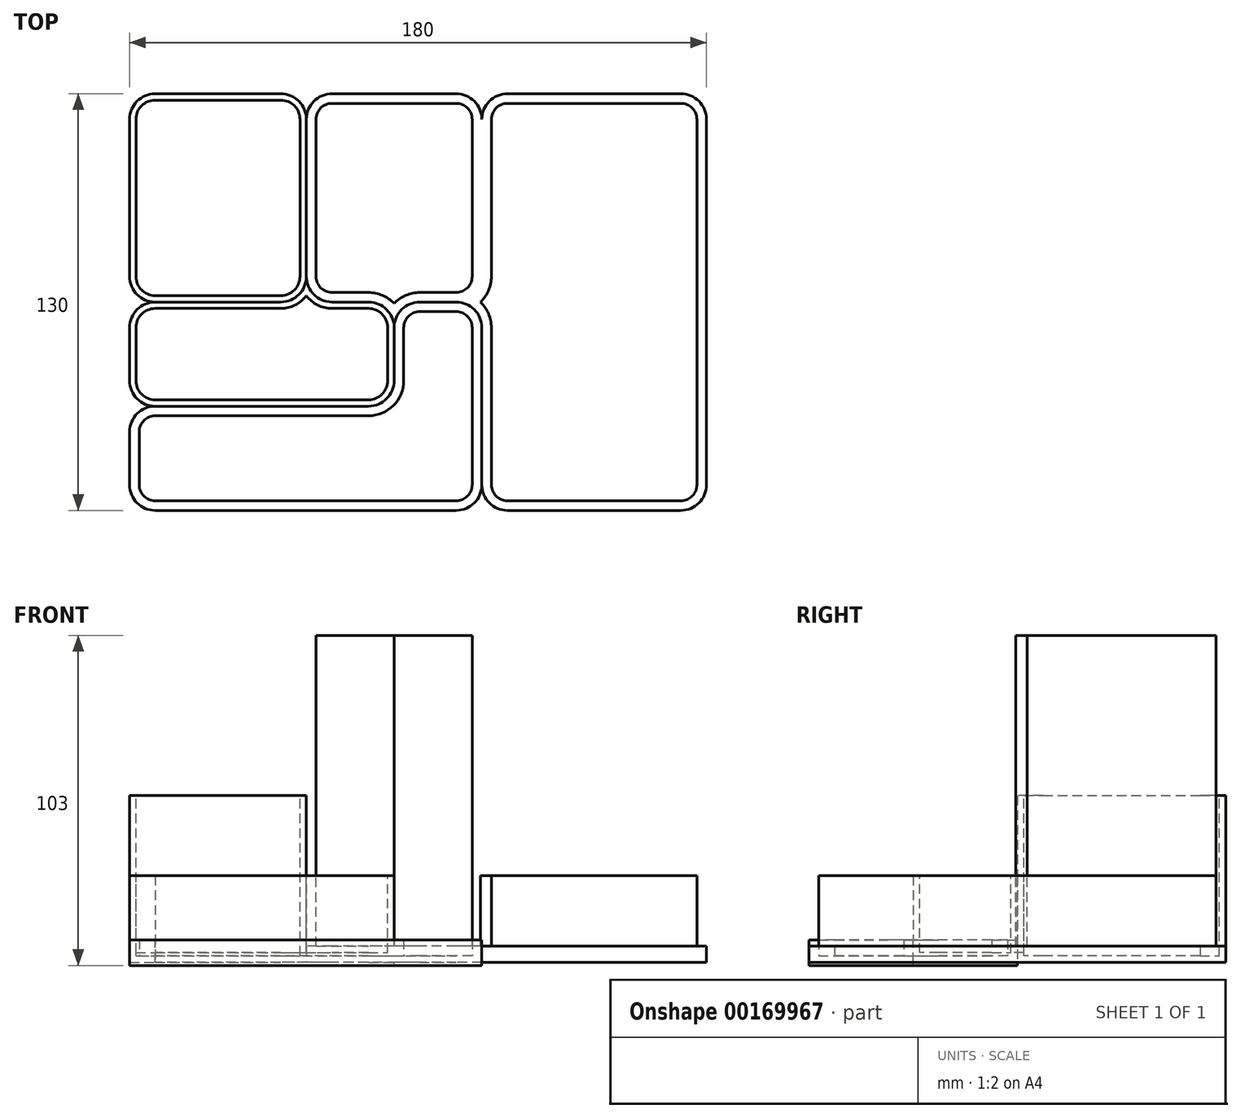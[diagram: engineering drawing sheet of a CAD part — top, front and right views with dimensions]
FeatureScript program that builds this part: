
annotation { "Feature Type Name" : "Feature", "Feature Type Description" : "" }
export const myFeature = defineFeature(function(context is Context, id is Id, definition is map)
    precondition{}
    {
        {
            var Q0;
            Q0=qCreatedBy(makeId("Top.planeOp"),FACE);
            var sketch = newSketch(context, id + "F0", { "sketchPlane" : qUnion([Q0])});
            skLineSegment(sketch, "E0.bottom", {"start": v(11.9, -65) * mm, "end": v(-82, -65) * mm});
            skLineSegment(sketch, "E0.top", {"start": v(82, 65) * mm, "end": v(27.9, 65) * mm});
            skLineSegment(sketch, "E0.left", {"start": v(90, -57) * mm, "end": v(90, 57) * mm});
            skLineSegment(sketch, "E0.right", {"start": v(-90, 8) * mm, "end": v(-90, 57) * mm});
            skPoint(sketch, "E0.middle", {"position": v(0, 0) * mm});
            skPoint(sketch, "E1.visualSharp", {"position": v(-90, 65) * mm});
            skArc(sketch, "E1.filletArc", {"start": v(-82, 65) * mm, "mid": v(-87.66, 62.66) * mm, "end": v(-90, 57) * mm});
            skPoint(sketch, "E2.visualSharp", {"position": v(90, 65) * mm});
            skArc(sketch, "E2.filletArc", {"start": v(90, 57) * mm, "mid": v(87.66, 62.66) * mm, "end": v(82, 65) * mm});
            skPoint(sketch, "E3.visualSharp", {"position": v(90, -65) * mm});
            skArc(sketch, "E3.filletArc", {"start": v(82, -65) * mm, "mid": v(87.66, -62.66) * mm, "end": v(90, -57) * mm});
            skPoint(sketch, "E4.visualSharp", {"position": v(-90, -65) * mm});
            skArc(sketch, "E4.filletArc", {"start": v(-90, -57) * mm, "mid": v(-87.66, -62.66) * mm, "end": v(-82, -65) * mm});
            skLineSegment(sketch, "E5", {"start": v(-34.83, 57) * mm, "end": v(-34.83, 8) * mm});
            skLineSegment(sketch, "E6", {"start": v(-82, 0) * mm, "end": v(-42.83, 0) * mm});
            skLineSegment(sketch, "E7", {"start": v(-26.83, 0) * mm, "end": v(-15.46, 0) * mm});
            skLineSegment(sketch, "E8", {"start": v(19.9, 8) * mm, "end": v(19.9, 57) * mm});
            skPoint(sketch, "E9.visualSharp", {"position": v(-34.83, 0) * mm});
            skArc(sketch, "E9.filletArc", {"start": v(-42.83, 0) * mm, "mid": v(-37.17, 2.34) * mm, "end": v(-34.83, 8) * mm});
            skArc(sketch, "E10.filletArc", {"start": v(-34.83, 8) * mm, "mid": v(-32.49, 2.34) * mm, "end": v(-26.83, 0) * mm});
            skPoint(sketch, "E11.visualSharp", {"position": v(19.9, 0) * mm});
            skArc(sketch, "E11.filletArc", {"start": v(11.9, 0) * mm, "mid": v(17.56, 2.34) * mm, "end": v(19.9, 8) * mm});
            skArc(sketch, "E12.filletArc", {"start": v(27.9, 65) * mm, "mid": v(22.24, 62.66) * mm, "end": v(19.9, 57) * mm});
            skLineSegment(sketch, "E13", {"start": v(-82, 65) * mm, "end": v(-42.83, 65) * mm});
            skArc(sketch, "E14.filletArc", {"start": v(19.9, 57) * mm, "mid": v(17.56, 62.66) * mm, "end": v(11.9, 65) * mm});
            skPoint(sketch, "E15.newPointA", {"position": v(-90, -57) * mm});
            skPoint(sketch, "E15.newPointB", {"position": v(-90, 0) * mm});
            skArc(sketch, "E15.filletArc", {"start": v(-90, 8) * mm, "mid": v(-87.66, 2.34) * mm, "end": v(-82, 0) * mm});
            skLineSegment(sketch, "E16", {"start": v(-90, -24.5) * mm, "end": v(-90, -8) * mm});
            skArc(sketch, "E17.filletArc", {"start": v(-82, 0) * mm, "mid": v(-87.66, -2.34) * mm, "end": v(-90, -8) * mm});
            skArc(sketch, "E18.filletArc", {"start": v(-34.83, 57) * mm, "mid": v(-37.17, 62.66) * mm, "end": v(-42.83, 65) * mm});
            skLineSegment(sketch, "E19", {"start": v(11.9, 65) * mm, "end": v(-26.83, 65) * mm});
            skArc(sketch, "E20.filletArc", {"start": v(-26.83, 65) * mm, "mid": v(-32.49, 62.66) * mm, "end": v(-34.83, 57) * mm});
            skLineSegment(sketch, "E21", {"start": v(-82, -32.5) * mm, "end": v(-15.46, -32.5) * mm});
            skPoint(sketch, "E22.visualSharp", {"position": v(19.9, -32.5) * mm});
            skPoint(sketch, "E23.newPointA", {"position": v(-90, -32.5) * mm});
            skArc(sketch, "E23.filletArc", {"start": v(-90, -24.5) * mm, "mid": v(-87.66, -30.16) * mm, "end": v(-82, -32.5) * mm});
            skLineSegment(sketch, "E24", {"start": v(-90, -57) * mm, "end": v(-90, -40.5) * mm});
            skArc(sketch, "E25.filletArc", {"start": v(-82, -32.5) * mm, "mid": v(-87.66, -34.84) * mm, "end": v(-90, -40.5) * mm});
            skLineSegment(sketch, "E26", {"start": v(-7.46, -8) * mm, "end": v(-7.46, -24.5) * mm});
            skPoint(sketch, "E27.visualSharp", {"position": v(-7.46, -32.5) * mm});
            skArc(sketch, "E27.filletArc", {"start": v(-15.46, -32.5) * mm, "mid": v(-9.8, -30.16) * mm, "end": v(-7.46, -24.5) * mm});
            skPoint(sketch, "E28.newPointA", {"position": v(-7.46, 0) * mm});
            skPoint(sketch, "E28.newPointB", {"position": v(11.9, 0) * mm});
            skArc(sketch, "E28.filletArc", {"start": v(-7.46, -8) * mm, "mid": v(-9.8, -2.34) * mm, "end": v(-15.46, 0) * mm});
            skLineSegment(sketch, "E29", {"start": v(11.9, 0) * mm, "end": v(0.54, 0) * mm});
            skArc(sketch, "E30.filletArc", {"start": v(0.54, 0) * mm, "mid": v(-5.12, -2.34) * mm, "end": v(-7.46, -8) * mm});
            skLineSegment(sketch, "E31", {"start": v(19.9, -8) * mm, "end": v(19.9, -57) * mm});
            skArc(sketch, "E32.filletArc", {"start": v(19.9, -8) * mm, "mid": v(17.56, -2.34) * mm, "end": v(11.9, 0) * mm});
            skArc(sketch, "E33.filletArc", {"start": v(11.9, -65) * mm, "mid": v(17.56, -62.66) * mm, "end": v(19.9, -57) * mm});
            skLineSegment(sketch, "E34", {"start": v(82, -65) * mm, "end": v(27.9, -65) * mm});
            skArc(sketch, "E35.filletArc", {"start": v(19.9, -57) * mm, "mid": v(22.24, -62.66) * mm, "end": v(27.9, -65) * mm});
            skSolve(sketch);
        }
        {
            var Q0;
            Q0=makeQuery(id+"F0.imprint","IMPRINT",FACE,{"disambiguationData":[TD([[makeQuery(id+"F0.imprint","IMPRINT",EDGE,{"derivedFrom":sQuery(id+"F0.wireOp",EDGE,"E0.bottom")}),-1.0]])]});
            extrude(context, id + "F1", {"entities" : qUnion([Q0]), "oppositeDirection" : true, "depth" : 3 * mm});
        }
        {
            var Q0;
            Q0=makeQuery(id+"F0.imprint","IMPRINT",FACE,{"disambiguationData":[TD([[makeQuery(id+"F0.imprint","IMPRINT",EDGE,{"derivedFrom":sQuery(id+"F0.wireOp",EDGE,"E0.right")}),-1.0]])]});
            extrude(context, id + "F2", {"entities" : qUnion([Q0]), "depth" : 50 * mm});
        }
        {
            var Q0;
            Q0=makeQuery(id+"F0.imprint","IMPRINT",FACE,{"disambiguationData":[TD([[makeQuery(id+"F0.imprint","IMPRINT",EDGE,{"derivedFrom":sQuery(id+"F0.wireOp",EDGE,"E5")}),1.0]])]});
            extrude(context, id + "F3", {"entities" : qUnion([Q0]), "operationType" : NewBodyOperationType.ADD, "depth" : 100 * mm});
        }
        {
            var Q0;
            Q0=makeQuery(id+"F0.imprint","IMPRINT",FACE,{"disambiguationData":[TD([[makeQuery(id+"F0.imprint","IMPRINT",EDGE,{"derivedFrom":sQuery(id+"F0.wireOp",EDGE,"E6")}),-1.0]])]});
            extrude(context, id + "F4", {"entities" : qUnion([Q0]), "operationType" : NewBodyOperationType.ADD, "depth" : 25 * mm});
        }
        {
            var Q0;
            Q0=makeQuery(id+"F0.imprint","IMPRINT",FACE,{"disambiguationData":[TD([[makeQuery(id+"F0.imprint","IMPRINT",EDGE,{"derivedFrom":sQuery(id+"F0.wireOp",EDGE,"E0.top")}),1.0]])]});
            extrude(context, id + "F5", {"entities" : qUnion([Q0]), "operationType" : NewBodyOperationType.ADD, "depth" : 25 * mm});
        }
        {
            var Q0;
            Q0=makeQuery(id+"F5.opExtrude","CAP_FACE",FACE,{"disambiguationData":[OSD([sQuery(id+"F0.wireOp",EDGE,"E0.top"),sQuery(id+"F0.wireOp",EDGE,"E0.left"),sQuery(id+"F0.wireOp",EDGE,"E2.filletArc"),sQuery(id+"F0.wireOp",EDGE,"E3.filletArc"),sQuery(id+"F0.wireOp",EDGE,"E8"),sQuery(id+"F0.wireOp",EDGE,"E11.filletArc"),sQuery(id+"F0.wireOp",EDGE,"E12.filletArc"),sQuery(id+"F0.wireOp",EDGE,"E31"),sQuery(id+"F0.wireOp",EDGE,"E32.filletArc"),sQuery(id+"F0.wireOp",EDGE,"E34"),sQuery(id+"F0.wireOp",EDGE,"E35.filletArc")])],"isStart":false});
            var sketch = newSketch(context, id + "F6", { "sketchPlane" : qUnion([Q0])});
            skArc(sketch, "E36.0", {"start": v(22.9, 8) * mm, "mid": v(22, 3.64) * mm, "end": v(19.45, 0) * mm});
            skLineSegment(sketch, "E36.1", {"start": v(22.9, 57) * mm, "end": v(22.9, 8) * mm});
            skArc(sketch, "E36.2", {"start": v(27.9, 62) * mm, "mid": v(24.37, 60.54) * mm, "end": v(22.9, 57) * mm});
            skLineSegment(sketch, "E36.3", {"start": v(82, 62) * mm, "end": v(27.9, 62) * mm});
            skArc(sketch, "E36.4", {"start": v(87, 57) * mm, "mid": v(85.54, 60.54) * mm, "end": v(82, 62) * mm});
            skArc(sketch, "E36.5", {"start": v(19.45, 0) * mm, "mid": v(22, -3.64) * mm, "end": v(22.9, -8) * mm});
            skLineSegment(sketch, "E36.6", {"start": v(22.9, -8) * mm, "end": v(22.9, -57) * mm});
            skArc(sketch, "E36.7", {"start": v(22.9, -57) * mm, "mid": v(24.37, -60.54) * mm, "end": v(27.9, -62) * mm});
            skLineSegment(sketch, "E36.8", {"start": v(27.9, -62) * mm, "end": v(82, -62) * mm});
            skArc(sketch, "E36.9", {"start": v(82, -62) * mm, "mid": v(85.54, -60.54) * mm, "end": v(87, -57) * mm});
            skLineSegment(sketch, "E36.10", {"start": v(87, -57) * mm, "end": v(87, 57) * mm});
            skSolve(sketch);
        }
        {
            var Q0;
            Q0=makeQuery(id+"F6.imprint","IMPRINT",FACE,{"disambiguationData":[TD([[makeQuery(id+"F6.imprint","IMPRINT",EDGE,{"derivedFrom":sQuery(id+"F6.wireOp",EDGE,"E36.0")}),1.0]])]});
            extrude(context, id + "F7", {"entities" : qUnion([Q0]), "operationType" : NewBodyOperationType.REMOVE, "oppositeDirection" : true, "depth" : 22 * mm});
        }
        {
            var Q0;
            Q0=makeQuery(id+"F0.imprint","IMPRINT",FACE,{"disambiguationData":[TD([[makeQuery(id+"F0.imprint","IMPRINT",EDGE,{"derivedFrom":sQuery(id+"F0.wireOp",EDGE,"E0.top")}),1.0]])]});
            var Q1;
            Q1=makeQuery(id+"F0.imprint","IMPRINT",FACE,{"disambiguationData":[TD([[makeQuery(id+"F0.imprint","IMPRINT",EDGE,{"derivedFrom":sQuery(id+"F0.wireOp",EDGE,"E5")}),1.0]])]});
            var Q2;
            Q2=makeQuery(id+"F0.imprint","IMPRINT",FACE,{"disambiguationData":[TD([[makeQuery(id+"F0.imprint","IMPRINT",EDGE,{"derivedFrom":sQuery(id+"F0.wireOp",EDGE,"E0.bottom")}),-1.0]])]});
            var Q3;
            Q3=makeQuery(id+"F0.imprint","IMPRINT",FACE,{"disambiguationData":[TD([[makeQuery(id+"F0.imprint","IMPRINT",EDGE,{"derivedFrom":sQuery(id+"F0.wireOp",EDGE,"E6")}),-1.0]])]});
            var Q4;
            Q4=makeQuery(id+"F0.imprint","IMPRINT",FACE,{"disambiguationData":[TD([[makeQuery(id+"F0.imprint","IMPRINT",EDGE,{"derivedFrom":sQuery(id+"F0.wireOp",EDGE,"E0.right")}),-1.0]])]});
            extrude(context, id + "F8", {"entities" : qUnion([Q0, Q1, Q2, Q3, Q4]), "operationType" : NewBodyOperationType.ADD, "oppositeDirection" : true, "depth" : 2 * mm});
        }
        {
            var Q0;
            Q0=makeQuery(id+"F3.opExtrude","CAP_FACE",FACE,{"disambiguationData":[OSD([sQuery(id+"F0.wireOp",EDGE,"E5"),sQuery(id+"F0.wireOp",EDGE,"E7"),sQuery(id+"F0.wireOp",EDGE,"E8"),sQuery(id+"F0.wireOp",EDGE,"E10.filletArc"),sQuery(id+"F0.wireOp",EDGE,"E11.filletArc"),sQuery(id+"F0.wireOp",EDGE,"E14.filletArc"),sQuery(id+"F0.wireOp",EDGE,"E19"),sQuery(id+"F0.wireOp",EDGE,"E20.filletArc"),sQuery(id+"F0.wireOp",EDGE,"E28.filletArc"),sQuery(id+"F0.wireOp",EDGE,"E29"),sQuery(id+"F0.wireOp",EDGE,"E30.filletArc")])],"isStart":false});
            var sketch = newSketch(context, id + "F9", { "sketchPlane" : qUnion([Q0])});
            skArc(sketch, "E37.0", {"start": v(-15.46, 3) * mm, "mid": v(-11.1, 2.1) * mm, "end": v(-7.46, -0.45) * mm});
            skLineSegment(sketch, "E37.1", {"start": v(-26.83, 3) * mm, "end": v(-15.46, 3) * mm});
            skArc(sketch, "E37.2", {"start": v(-31.83, 8) * mm, "mid": v(-30.37, 4.46) * mm, "end": v(-26.83, 3) * mm});
            skLineSegment(sketch, "E37.3", {"start": v(-31.83, 57) * mm, "end": v(-31.83, 8) * mm});
            skArc(sketch, "E37.4", {"start": v(-26.83, 62) * mm, "mid": v(-30.37, 60.54) * mm, "end": v(-31.83, 57) * mm});
            skArc(sketch, "E37.5", {"start": v(-7.46, -0.45) * mm, "mid": v(-3.82, 2.1) * mm, "end": v(0.54, 3) * mm});
            skLineSegment(sketch, "E37.6", {"start": v(0.54, 3) * mm, "end": v(11.9, 3) * mm});
            skArc(sketch, "E37.7", {"start": v(11.9, 3) * mm, "mid": v(15.44, 4.46) * mm, "end": v(16.9, 8) * mm});
            skLineSegment(sketch, "E37.8", {"start": v(16.9, 8) * mm, "end": v(16.9, 57) * mm});
            skArc(sketch, "E37.9", {"start": v(16.9, 57) * mm, "mid": v(15.44, 60.54) * mm, "end": v(11.9, 62) * mm});
            skLineSegment(sketch, "E37.10", {"start": v(11.9, 62) * mm, "end": v(-26.83, 62) * mm});
            skSolve(sketch);
        }
        {
            var Q0;
            Q0=makeQuery(id+"F9.imprint","IMPRINT",FACE,{"disambiguationData":[TD([[makeQuery(id+"F9.imprint","IMPRINT",EDGE,{"derivedFrom":sQuery(id+"F9.wireOp",EDGE,"E37.0")}),1.0]])]});
            extrude(context, id + "F10", {"entities" : qUnion([Q0]), "operationType" : NewBodyOperationType.REMOVE, "oppositeDirection" : true, "offsetDistance" : 25 * mm, "depth" : 97 * mm});
        }
        {
            var Q0;
            Q0=makeQuery(id+"F2.opExtrude","CAP_FACE",FACE,{"disambiguationData":[OSD([sQuery(id+"F0.wireOp",EDGE,"E0.right"),sQuery(id+"F0.wireOp",EDGE,"E1.filletArc"),sQuery(id+"F0.wireOp",EDGE,"E5"),sQuery(id+"F0.wireOp",EDGE,"E6"),sQuery(id+"F0.wireOp",EDGE,"E9.filletArc"),sQuery(id+"F0.wireOp",EDGE,"E13"),sQuery(id+"F0.wireOp",EDGE,"E15.filletArc"),sQuery(id+"F0.wireOp",EDGE,"E18.filletArc")])],"isStart":false});
            var sketch = newSketch(context, id + "F11", { "sketchPlane" : qUnion([Q0])});
            skArc(sketch, "E38.0", {"start": v(-88, 8) * mm, "mid": v(-86.24, 3.76) * mm, "end": v(-82, 2) * mm});
            skLineSegment(sketch, "E38.1", {"start": v(-88, 57) * mm, "end": v(-88, 8) * mm});
            skLineSegment(sketch, "E38.2", {"start": v(-82, 2) * mm, "end": v(-42.83, 2) * mm});
            skArc(sketch, "E38.3", {"start": v(-82, 63) * mm, "mid": v(-86.24, 61.24) * mm, "end": v(-88, 57) * mm});
            skArc(sketch, "E38.4", {"start": v(-42.83, 2) * mm, "mid": v(-38.59, 3.76) * mm, "end": v(-36.83, 8) * mm});
            skLineSegment(sketch, "E38.5", {"start": v(-36.83, 8) * mm, "end": v(-36.83, 57) * mm});
            skArc(sketch, "E38.6", {"start": v(-36.83, 57) * mm, "mid": v(-38.59, 61.24) * mm, "end": v(-42.83, 63) * mm});
            skLineSegment(sketch, "E38.7", {"start": v(-42.83, 63) * mm, "end": v(-82, 63) * mm});
            skSolve(sketch);
        }
        {
            var Q0;
            Q0=makeQuery(id+"F11.imprint","IMPRINT",FACE,{"disambiguationData":[TD([[makeQuery(id+"F11.imprint","IMPRINT",EDGE,{"derivedFrom":sQuery(id+"F11.wireOp",EDGE,"E38.0")}),1.0]])]});
            extrude(context, id + "F12", {"entities" : qUnion([Q0]), "operationType" : NewBodyOperationType.REMOVE, "oppositeDirection" : true, "depth" : 50 * mm, "offsetDistance" : 25 * mm});
        }
        {
            var Q0;
            Q0=makeQuery(id+"F4.opExtrude","CAP_FACE",FACE,{"disambiguationData":[OSD([sQuery(id+"F0.wireOp",EDGE,"E6"),sQuery(id+"F0.wireOp",EDGE,"E7"),sQuery(id+"F0.wireOp",EDGE,"E9.filletArc"),sQuery(id+"F0.wireOp",EDGE,"E10.filletArc"),sQuery(id+"F0.wireOp",EDGE,"E16"),sQuery(id+"F0.wireOp",EDGE,"E17.filletArc"),sQuery(id+"F0.wireOp",EDGE,"E21"),sQuery(id+"F0.wireOp",EDGE,"E23.filletArc"),sQuery(id+"F0.wireOp",EDGE,"E26"),sQuery(id+"F0.wireOp",EDGE,"E27.filletArc"),sQuery(id+"F0.wireOp",EDGE,"E28.filletArc")])],"isStart":false});
            var sketch = newSketch(context, id + "F13", { "sketchPlane" : qUnion([Q0])});
            skArc(sketch, "E39.0", {"start": v(-88, -24.5) * mm, "mid": v(-86.24, -28.74) * mm, "end": v(-82, -30.5) * mm});
            skLineSegment(sketch, "E39.1", {"start": v(-88, -8) * mm, "end": v(-88, -24.5) * mm});
            skArc(sketch, "E39.2", {"start": v(-82, -2) * mm, "mid": v(-86.24, -3.76) * mm, "end": v(-88, -8) * mm});
            skLineSegment(sketch, "E39.3", {"start": v(-42.83, -2) * mm, "end": v(-82, -2) * mm});
            skArc(sketch, "E39.4", {"start": v(-34.83, 2) * mm, "mid": v(-38.36, -0.94) * mm, "end": v(-42.83, -2) * mm});
            skLineSegment(sketch, "E39.5", {"start": v(-82, -30.5) * mm, "end": v(-15.46, -30.5) * mm});
            skArc(sketch, "E39.6", {"start": v(-15.46, -30.5) * mm, "mid": v(-11.22, -28.74) * mm, "end": v(-9.46, -24.5) * mm});
            skLineSegment(sketch, "E39.7", {"start": v(-9.46, -24.5) * mm, "end": v(-9.46, -8) * mm});
            skArc(sketch, "E39.8", {"start": v(-9.46, -8) * mm, "mid": v(-11.22, -3.76) * mm, "end": v(-15.46, -2) * mm});
            skLineSegment(sketch, "E39.9", {"start": v(-15.46, -2) * mm, "end": v(-26.83, -2) * mm});
            skArc(sketch, "E39.10", {"start": v(-26.83, -2) * mm, "mid": v(-31.3, -0.94) * mm, "end": v(-34.83, 2) * mm});
            skSolve(sketch);
        }
        {
            var Q0;
            Q0=makeQuery(id+"F13.imprint","IMPRINT",FACE,{"disambiguationData":[TD([[makeQuery(id+"F13.imprint","IMPRINT",EDGE,{"derivedFrom":sQuery(id+"F13.wireOp",EDGE,"E39.0")}),1.0]])]});
            extrude(context, id + "F14", {"entities" : qUnion([Q0]), "operationType" : NewBodyOperationType.REMOVE, "oppositeDirection" : true, "depth" : 24 * mm, "offsetDistance" : 25 * mm});
        }
        {
            var Q0;
            Q0=makeQuery(id+"F1.opExtrude","CAP_FACE",FACE,{"disambiguationData":[OSD([sQuery(id+"F0.wireOp",EDGE,"E0.bottom"),sQuery(id+"F0.wireOp",EDGE,"E4.filletArc"),sQuery(id+"F0.wireOp",EDGE,"E21"),sQuery(id+"F0.wireOp",EDGE,"E24"),sQuery(id+"F0.wireOp",EDGE,"E25.filletArc"),sQuery(id+"F0.wireOp",EDGE,"E26"),sQuery(id+"F0.wireOp",EDGE,"E27.filletArc"),sQuery(id+"F0.wireOp",EDGE,"E29"),sQuery(id+"F0.wireOp",EDGE,"E30.filletArc"),sQuery(id+"F0.wireOp",EDGE,"E31"),sQuery(id+"F0.wireOp",EDGE,"E32.filletArc"),sQuery(id+"F0.wireOp",EDGE,"E33.filletArc")])],"isStart":true});
            var sketch = newSketch(context, id + "F15", { "sketchPlane" : qUnion([Q0])});
            skArc(sketch, "E40.0", {"start": v(11.9, -62) * mm, "mid": v(15.44, -60.54) * mm, "end": v(16.9, -57) * mm});
            skLineSegment(sketch, "E40.1", {"start": v(-4.46, -8) * mm, "end": v(-4.46, -24.5) * mm});
            skArc(sketch, "E40.2", {"start": v(0.54, -3) * mm, "mid": v(-3, -4.46) * mm, "end": v(-4.46, -8) * mm});
            skLineSegment(sketch, "E40.3", {"start": v(11.9, -3) * mm, "end": v(0.54, -3) * mm});
            skArc(sketch, "E40.4", {"start": v(16.9, -8) * mm, "mid": v(15.44, -4.46) * mm, "end": v(11.9, -3) * mm});
            skArc(sketch, "E40.5", {"start": v(-4.46, -24.5) * mm, "mid": v(-7.69, -32.28) * mm, "end": v(-15.46, -35.5) * mm});
            skLineSegment(sketch, "E40.6", {"start": v(16.9, -57) * mm, "end": v(16.9, -8) * mm});
            skLineSegment(sketch, "E40.7", {"start": v(-15.46, -35.5) * mm, "end": v(-82, -35.5) * mm});
            skArc(sketch, "E40.8", {"start": v(-82, -35.5) * mm, "mid": v(-85.54, -36.96) * mm, "end": v(-87, -40.5) * mm});
            skLineSegment(sketch, "E40.9", {"start": v(-87, -40.5) * mm, "end": v(-87, -57) * mm});
            skArc(sketch, "E40.10", {"start": v(-87, -57) * mm, "mid": v(-85.54, -60.54) * mm, "end": v(-82, -62) * mm});
            skLineSegment(sketch, "E40.11", {"start": v(-82, -62) * mm, "end": v(11.9, -62) * mm});
            skSolve(sketch);
        }
        {
            var Q0;
            Q0=makeQuery(id+"F15.imprint","IMPRINT",FACE,{"disambiguationData":[TD([[makeQuery(id+"F15.imprint","IMPRINT",EDGE,{"derivedFrom":sQuery(id+"F15.wireOp",EDGE,"E40.0")}),-1.0]])]});
            extrude(context, id + "F16", {"entities" : qUnion([Q0]), "operationType" : NewBodyOperationType.ADD, "depth" : 5 * mm, "offsetDistance" : 25 * mm});
        }
    });
